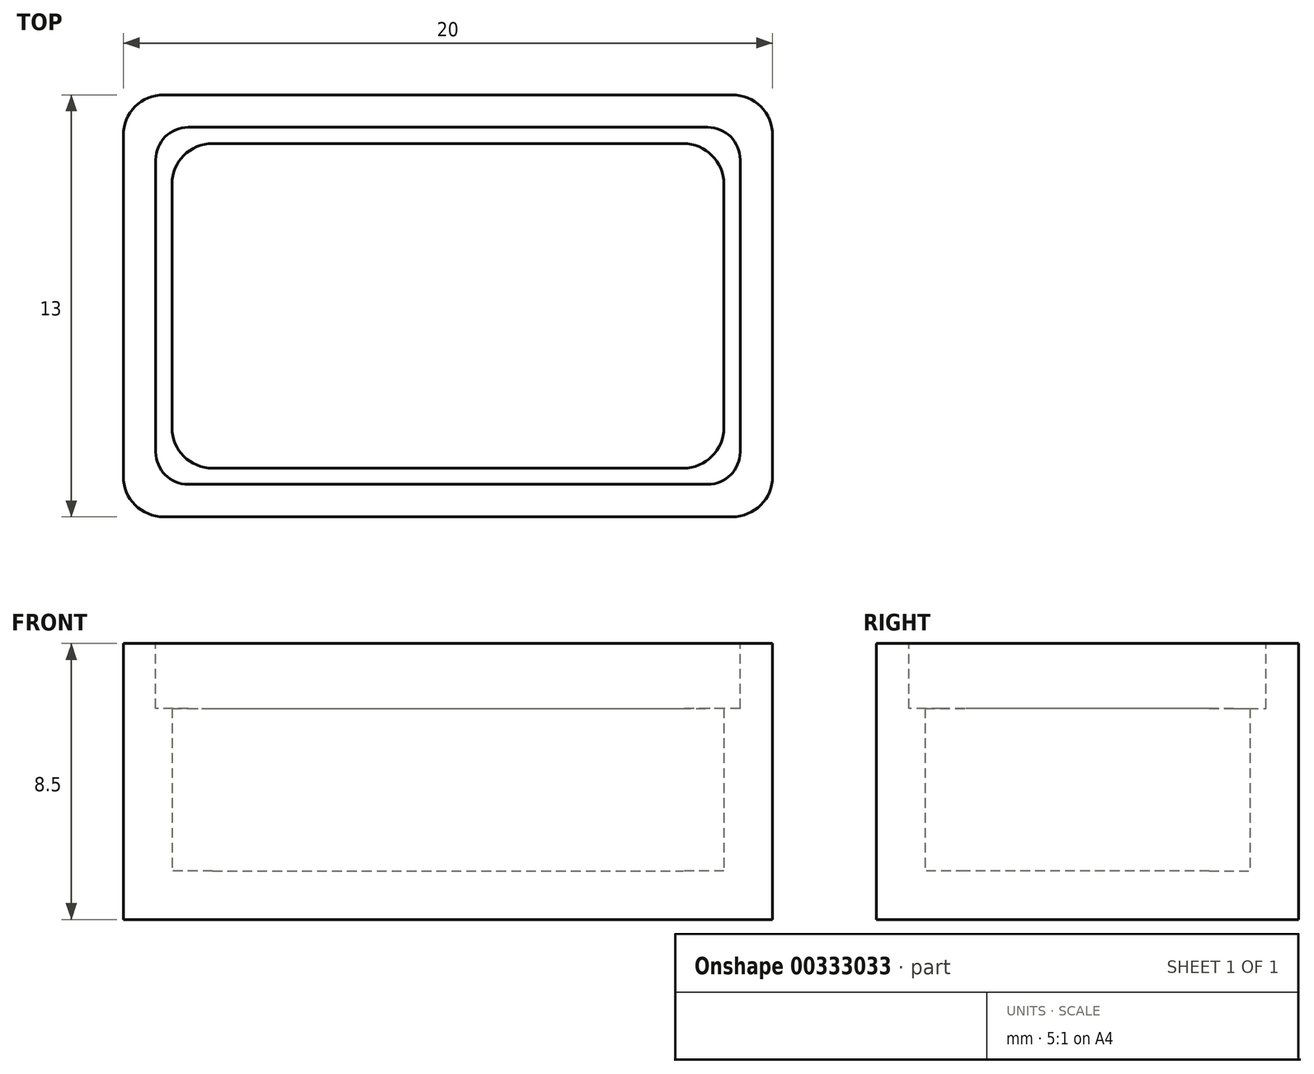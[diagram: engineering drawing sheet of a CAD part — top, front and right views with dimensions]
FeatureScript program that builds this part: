
annotation { "Feature Type Name" : "Feature", "Feature Type Description" : "" }
export const myFeature = defineFeature(function(context is Context, id is Id, definition is map)
    precondition{}
    {
        {
            var Q0;
            Q0=qCreatedBy(makeId("Top.planeOp"),FACE);
            var sketch = newSketch(context, id + "F0", { "sketchPlane" : qUnion([Q0])});
            skLineSegment(sketch, "E0.bottom", {"start": v(-8.75, 6.5) * mm, "end": v(8.75, 6.5) * mm});
            skLineSegment(sketch, "E0.top", {"start": v(-8.75, -6.5) * mm, "end": v(8.75, -6.5) * mm});
            skLineSegment(sketch, "E0.left", {"start": v(-10, 5.25) * mm, "end": v(-10, -5.25) * mm});
            skLineSegment(sketch, "E0.right", {"start": v(10, 5.25) * mm, "end": v(10, -5.25) * mm});
            skPoint(sketch, "E0.middle", {"position": v(0, 0) * mm});
            skPoint(sketch, "E1.visualSharp", {"position": v(-10, 6.5) * mm});
            skArc(sketch, "E1.filletArc", {"start": v(-8.75, 6.5) * mm, "mid": v(-9.63, 6.13) * mm, "end": v(-10, 5.25) * mm});
            skPoint(sketch, "E2.visualSharp", {"position": v(10, 6.5) * mm});
            skArc(sketch, "E2.filletArc", {"start": v(10, 5.25) * mm, "mid": v(9.63, 6.13) * mm, "end": v(8.75, 6.5) * mm});
            skPoint(sketch, "E3.visualSharp", {"position": v(10, -6.5) * mm});
            skArc(sketch, "E3.filletArc", {"start": v(8.75, -6.5) * mm, "mid": v(9.63, -6.13) * mm, "end": v(10, -5.25) * mm});
            skPoint(sketch, "E4.visualSharp", {"position": v(-10, -6.5) * mm});
            skArc(sketch, "E4.filletArc", {"start": v(-10, -5.25) * mm, "mid": v(-9.63, -6.13) * mm, "end": v(-8.75, -6.5) * mm});
            skSolve(sketch);
        }
        {
            var Q0;
            Q0 = qSketchRegion(id + "F0", true);
            extrude(context, id + "F1", {"entities" : qUnion([Q0]), "depth" : 1.5 * mm});
        }
        {
            var Q0;
            Q0=makeQuery(id+"F1.opExtrude","CAP_FACE",FACE,{"disambiguationData":[OSD([sQuery(id+"F0.wireOp",EDGE,"E0.bottom"),sQuery(id+"F0.wireOp",EDGE,"E0.top"),sQuery(id+"F0.wireOp",EDGE,"E0.left"),sQuery(id+"F0.wireOp",EDGE,"E0.right"),sQuery(id+"F0.wireOp",EDGE,"E1.filletArc"),sQuery(id+"F0.wireOp",EDGE,"E2.filletArc"),sQuery(id+"F0.wireOp",EDGE,"E3.filletArc"),sQuery(id+"F0.wireOp",EDGE,"E4.filletArc")])],"isStart":false});
            var sketch = newSketch(context, id + "F2", { "sketchPlane" : qUnion([Q0])});
            skLineSegment(sketch, "E5.bottom", {"start": v(-7.25, 5) * mm, "end": v(7.25, 5) * mm});
            skLineSegment(sketch, "E5.top", {"start": v(-7.25, -5) * mm, "end": v(7.25, -5) * mm});
            skLineSegment(sketch, "E5.left", {"start": v(-8.5, 3.75) * mm, "end": v(-8.5, -3.75) * mm});
            skLineSegment(sketch, "E5.right", {"start": v(8.5, 3.75) * mm, "end": v(8.5, -3.75) * mm});
            skPoint(sketch, "E5.middle", {"position": v(0, 0) * mm});
            skPoint(sketch, "E6.visualSharp", {"position": v(-8.5, 5) * mm});
            skArc(sketch, "E6.filletArc", {"start": v(-7.25, 5) * mm, "mid": v(-8.13, 4.63) * mm, "end": v(-8.5, 3.75) * mm});
            skPoint(sketch, "E7.visualSharp", {"position": v(8.5, 5) * mm});
            skArc(sketch, "E7.filletArc", {"start": v(8.5, 3.75) * mm, "mid": v(8.13, 4.63) * mm, "end": v(7.25, 5) * mm});
            skPoint(sketch, "E8.visualSharp", {"position": v(8.5, -5) * mm});
            skArc(sketch, "E8.filletArc", {"start": v(7.25, -5) * mm, "mid": v(8.13, -4.63) * mm, "end": v(8.5, -3.75) * mm});
            skPoint(sketch, "E9.visualSharp", {"position": v(-8.5, -5) * mm});
            skArc(sketch, "E9.filletArc", {"start": v(-8.5, -3.75) * mm, "mid": v(-8.13, -4.63) * mm, "end": v(-7.25, -5) * mm});
            skSolve(sketch);
        }
        {
            var Q0;
            Q0=makeQuery(id+"F2.imprint","IMPRINT",FACE,{"disambiguationData":[TD([[makeQuery(id+"F2.imprint","IMPRINT",EDGE,{"derivedFrom":sQuery(id+"F2.wireOp",EDGE,"E5.bottom")}),1.0]])]});
            extrude(context, id + "F3", {"entities" : qUnion([Q0]), "operationType" : NewBodyOperationType.ADD, "depth" : 7 * mm});
        }
        {
            var Q0;
            Q0=makeQuery(id+"F3.opExtrude","CAP_FACE",FACE,{"disambiguationData":[OSD([sQuery(id+"F0.wireOp",EDGE,"E0.bottom"),sQuery(id+"F0.wireOp",EDGE,"E0.top"),sQuery(id+"F0.wireOp",EDGE,"E0.left"),sQuery(id+"F0.wireOp",EDGE,"E0.right"),sQuery(id+"F0.wireOp",EDGE,"E1.filletArc"),sQuery(id+"F0.wireOp",EDGE,"E2.filletArc"),sQuery(id+"F0.wireOp",EDGE,"E3.filletArc"),sQuery(id+"F0.wireOp",EDGE,"E4.filletArc"),sQuery(id+"F2.wireOp",EDGE,"E5.bottom"),sQuery(id+"F2.wireOp",EDGE,"E5.top"),sQuery(id+"F2.wireOp",EDGE,"E5.left"),sQuery(id+"F2.wireOp",EDGE,"E5.right"),sQuery(id+"F2.wireOp",EDGE,"E6.filletArc"),sQuery(id+"F2.wireOp",EDGE,"E7.filletArc"),sQuery(id+"F2.wireOp",EDGE,"E8.filletArc"),sQuery(id+"F2.wireOp",EDGE,"E9.filletArc")])],"isStart":false});
            var sketch = newSketch(context, id + "F4", { "sketchPlane" : qUnion([Q0])});
            skLineSegment(sketch, "E10.bottom", {"start": v(-8, 5.5) * mm, "end": v(8, 5.5) * mm});
            skLineSegment(sketch, "E10.top", {"start": v(-8, -5.5) * mm, "end": v(8, -5.5) * mm});
            skLineSegment(sketch, "E10.left", {"start": v(-9, 4.5) * mm, "end": v(-9, -4.5) * mm});
            skLineSegment(sketch, "E10.right", {"start": v(9, 4.5) * mm, "end": v(9, -4.5) * mm});
            skPoint(sketch, "E10.middle", {"position": v(0, 0) * mm});
            skPoint(sketch, "E11.visualSharp", {"position": v(-9, 5.5) * mm});
            skArc(sketch, "E11.filletArc", {"start": v(-8, 5.5) * mm, "mid": v(-8.7, 5.2) * mm, "end": v(-9, 4.5) * mm});
            skPoint(sketch, "E12.visualSharp", {"position": v(9, 5.5) * mm});
            skArc(sketch, "E12.filletArc", {"start": v(9, 4.5) * mm, "mid": v(8.7, 5.2) * mm, "end": v(8, 5.5) * mm});
            skPoint(sketch, "E13.visualSharp", {"position": v(9, -5.5) * mm});
            skArc(sketch, "E13.filletArc", {"start": v(8, -5.5) * mm, "mid": v(8.7, -5.2) * mm, "end": v(9, -4.5) * mm});
            skPoint(sketch, "E14.visualSharp", {"position": v(-9, -5.5) * mm});
            skArc(sketch, "E14.filletArc", {"start": v(-9, -4.5) * mm, "mid": v(-8.7, -5.2) * mm, "end": v(-8, -5.5) * mm});
            skSolve(sketch);
        }
        {
            var Q0;
            Q0=makeQuery(id+"F4.imprint","IMPRINT",FACE,{"disambiguationData":[TD([[makeQuery(id+"F4.imprint","IMPRINT",EDGE,{"derivedFrom":sQuery(id+"F4.wireOp",EDGE,"E10.bottom")}),-1.0]])]});
            extrude(context, id + "F5", {"entities" : qUnion([Q0]), "operationType" : NewBodyOperationType.REMOVE, "oppositeDirection" : true, "depth" : 2 * mm});
        }
    });
